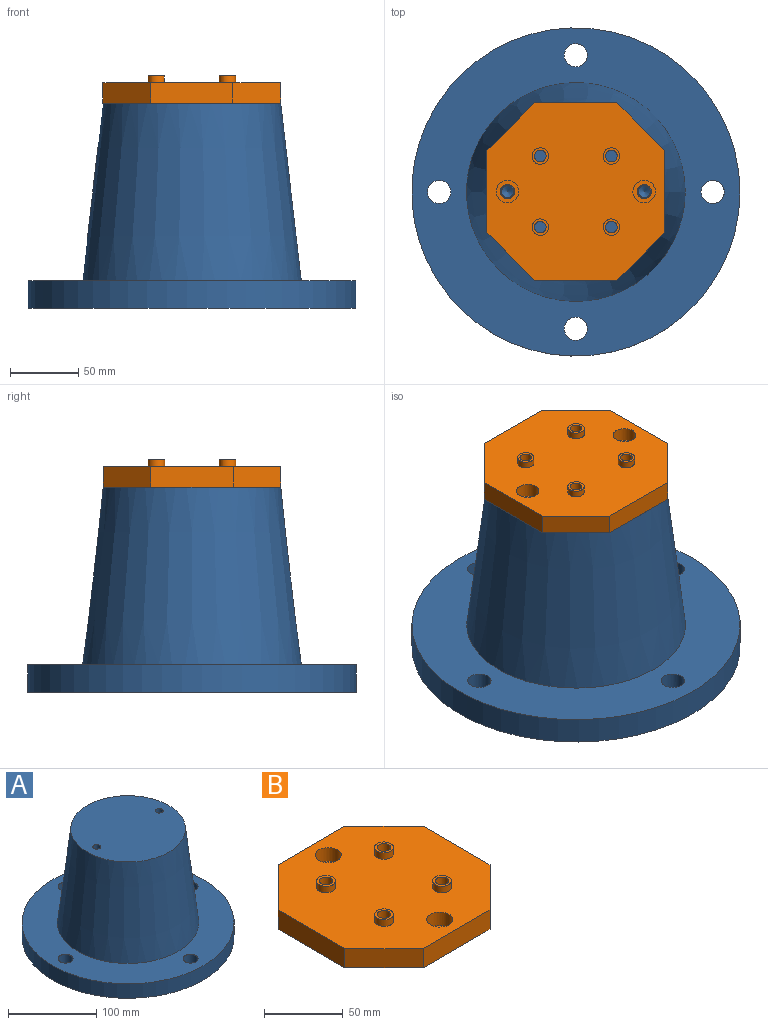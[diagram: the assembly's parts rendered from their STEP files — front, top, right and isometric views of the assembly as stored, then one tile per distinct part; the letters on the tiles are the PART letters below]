
ASSEMBLY  parts=2 mates=1
PART A: 13 faces, bbox 240x240x150 mm
  f0: plane 130x130mm, normal (0,0,1), area 13151.6mm2, adj f1,f10,f12
  f1: cone r=80mm half-angle=6.6deg, axis (0,0,-1), area 59611.9mm2, adj f0,f2
  f2: plane 240x240mm, normal (0,0,1), area 24224.8mm2, adj f1,f3,f5,f6,f7,f8
  f3: cylinder r=120mm len=240mm, axis (0,0,1), area 15079.6mm2, adj f2,f4
  f4: plane 240x240mm, normal (0,0,-1), area 44331mm2, adj f3,f5,f6,f7,f8
  f5: cylinder r=8.5mm len=20mm, axis (0,0,-1), area 1068.1mm2, adj f2,f4
  f6: cylinder r=8.5mm len=20mm, axis (0,0,-1), area 1068.1mm2, adj f2,f4
  f7: cylinder r=8.5mm len=20mm, axis (0,0,-1), area 1068.1mm2, adj f2,f4
  f8: cylinder r=8.5mm len=20mm, axis (0,0,-1), area 1068.1mm2, adj f2,f4
  f9: cone r=0mm half-angle=59deg, axis (0,0,1), area 71mm2, adj f10
  f10: cylinder r=4.4mm len=25mm, axis (0,0,1), area 691.2mm2, adj f0,f9
  f11: cone r=0mm half-angle=59deg, axis (0,0,1), area 71mm2, adj f12
  f12: cylinder r=4.4mm len=25mm, axis (0,0,1), area 691.2mm2, adj f0,f11
PART B: 36 faces, bbox 130x130x20 mm
  f0: plane 130x130mm, normal (0,0,1), area 13570mm2, adj f6,f7,f8,f9,f10,f12,f14,f16
  f1: plane 130x130mm, normal (0,0,-1), area 13704.3mm2, adj f6,f7,f8,f9,f19,f20,f23,f24
  f2: cylinder r=4.25mm len=11.5mm, axis (0,0,1), area 307.1mm2, adj f13,f25
  f3: cylinder r=4.25mm len=11.5mm, axis (0,0,1), area 307.1mm2, adj f17,f22
  f4: cylinder r=4.25mm len=11.5mm, axis (0,0,1), area 307.1mm2, adj f15,f21
  f5: cylinder r=4.25mm len=11.5mm, axis (0,0,1), area 307.1mm2, adj f11,f18
  f6: plane 60x15mm, normal (0,1,0), area 900mm2, adj f0,f1,f28,f29
  f7: plane 60x15mm, normal (-1,0,0), area 900mm2, adj f0,f1,f26,f29
  f8: plane 60x15mm, normal (0,-1,0), area 900mm2, adj f0,f1,f26,f27
  f9: plane 60x15mm, normal (1,0,0), area 900mm2, adj f0,f1,f27,f28
  f10: cylinder r=6mm len=12mm, axis (0,0,-1), area 188.5mm2, adj f0,f11
  f11: plane 12x12mm, normal (0,0,1), area 56.4mm2, adj f5,f10
  f12: cylinder r=6mm len=12mm, axis (0,0,-1), area 188.5mm2, adj f0,f13
  f13: plane 12x12mm, normal (0,0,1), area 56.4mm2, adj f2,f12
  f14: cylinder r=6mm len=12mm, axis (0,0,-1), area 188.5mm2, adj f0,f15
  f15: plane 12x12mm, normal (0,0,1), area 56.4mm2, adj f4,f14
  f16: cylinder r=6mm len=12mm, axis (0,0,-1), area 188.5mm2, adj f0,f17
  f17: plane 12x12mm, normal (0,0,1), area 56.4mm2, adj f3,f16
  f18: plane 13.5x13.5mm, normal (0,0,-1), area 86.4mm2, adj f5,f19
  f19: cylinder r=6.75mm len=13.5mm, axis (0,0,-1), area 360.5mm2, adj f1,f18
  f20: cylinder r=6.75mm len=13.5mm, axis (0,0,-1), area 360.5mm2, adj f1,f21
  f21: plane 13.5x13.5mm, normal (0,0,-1), area 86.4mm2, adj f4,f20
  f22: plane 13.5x13.5mm, normal (0,0,-1), area 86.4mm2, adj f3,f23
  f23: cylinder r=6.75mm len=13.5mm, axis (0,0,-1), area 360.5mm2, adj f1,f22
  f24: cylinder r=6.75mm len=13.5mm, axis (0,0,-1), area 360.5mm2, adj f1,f25
  f25: plane 13.5x13.5mm, normal (0,0,-1), area 86.4mm2, adj f2,f24
  f26: plane 35x35mm, normal (-0.71,-0.71,0), area 742.5mm2, adj f0,f1,f7,f8
  f27: plane 35x35mm, normal (0.71,-0.71,0), area 742.5mm2, adj f0,f1,f8,f9
  f28: plane 35x35mm, normal (0.71,0.71,0), area 742.5mm2, adj f0,f1,f6,f9
  f29: plane 35x35mm, normal (-0.71,0.71,0), area 742.5mm2, adj f0,f1,f6,f7
  f30: cylinder r=5.25mm len=10.5mm, axis (0,0,1), area 148.4mm2, adj f1,f35
  f31: cylinder r=5.25mm len=10.5mm, axis (0,0,1), area 148.4mm2, adj f1,f33
  f32: cylinder r=8.25mm len=16.5mm, axis (0,0,1), area 544.3mm2, adj f0,f33
  f33: plane 16.5x16.5mm, normal (0,0,1), area 127.2mm2, adj f31,f32
  f34: cylinder r=8.25mm len=16.5mm, axis (0,0,1), area 544.3mm2, adj f0,f35
  f35: plane 16.5x16.5mm, normal (0,0,1), area 127.2mm2, adj f30,f34
PLACE A t=(-201.13,174.6,-66.91)mm
PLACE B rot(axis=(0,0,-1),90deg) t=(-201.13,174.6,83.09)mm
MATE cylindrical B.f30 <-> A.f11  axis (0,0,-1) through (-251.13,174.6,83.09)mm
